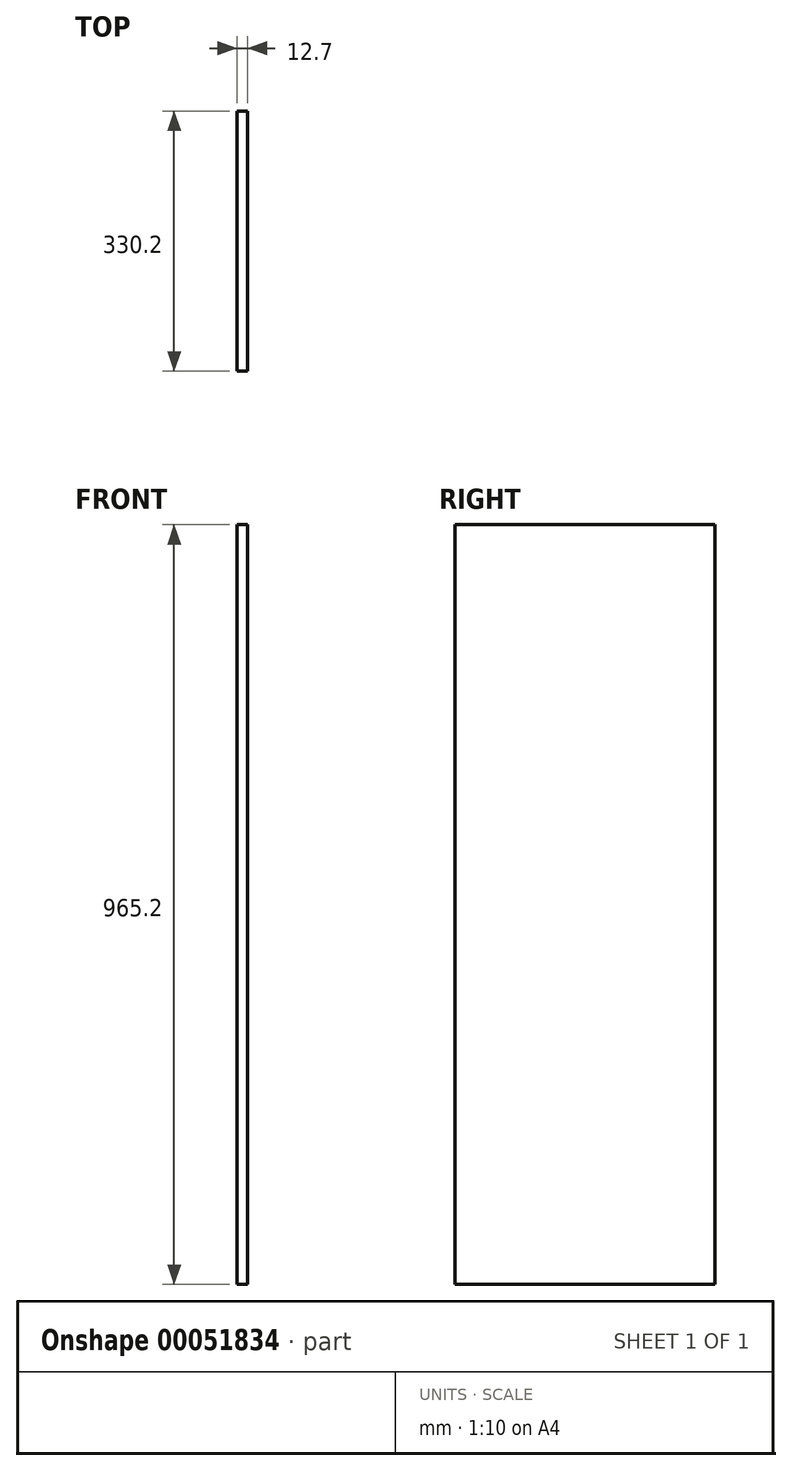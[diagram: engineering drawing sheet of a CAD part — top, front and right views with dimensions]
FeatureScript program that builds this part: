
annotation { "Feature Type Name" : "Feature", "Feature Type Description" : "" }
export const myFeature = defineFeature(function(context is Context, id is Id, definition is map)
    precondition{}
    {
        {
            var Q0;
            Q0=qCreatedBy(makeId("Right.planeOp"),FACE);
            var sketch = newSketch(context, id + "F0", { "sketchPlane" : qUnion([Q0])});
            skLineSegment(sketch, "E0.bottom", {"start": v(-165.1, -482.6) * mm, "end": v(165.1, -482.6) * mm});
            skLineSegment(sketch, "E0.top", {"start": v(-165.1, 482.6) * mm, "end": v(165.1, 482.6) * mm});
            skLineSegment(sketch, "E0.left", {"start": v(-165.1, -482.6) * mm, "end": v(-165.1, 482.6) * mm});
            skLineSegment(sketch, "E0.right", {"start": v(165.1, -482.6) * mm, "end": v(165.1, 482.6) * mm});
            skSolve(sketch);
        }
        {
            var Q0;
            Q0=makeQuery(id+"F0.imprint","IMPRINT",FACE,{"disambiguationData":[TD([[makeQuery(id+"F0.imprint","IMPRINT",EDGE,{"derivedFrom":sQuery(id+"F0.wireOp",EDGE,"E0.bottom")}),1.0]])]});
            extrude(context, id + "F1", {"entities" : qUnion([Q0]), "depth" : 12.7 * mm});
        }
    });
